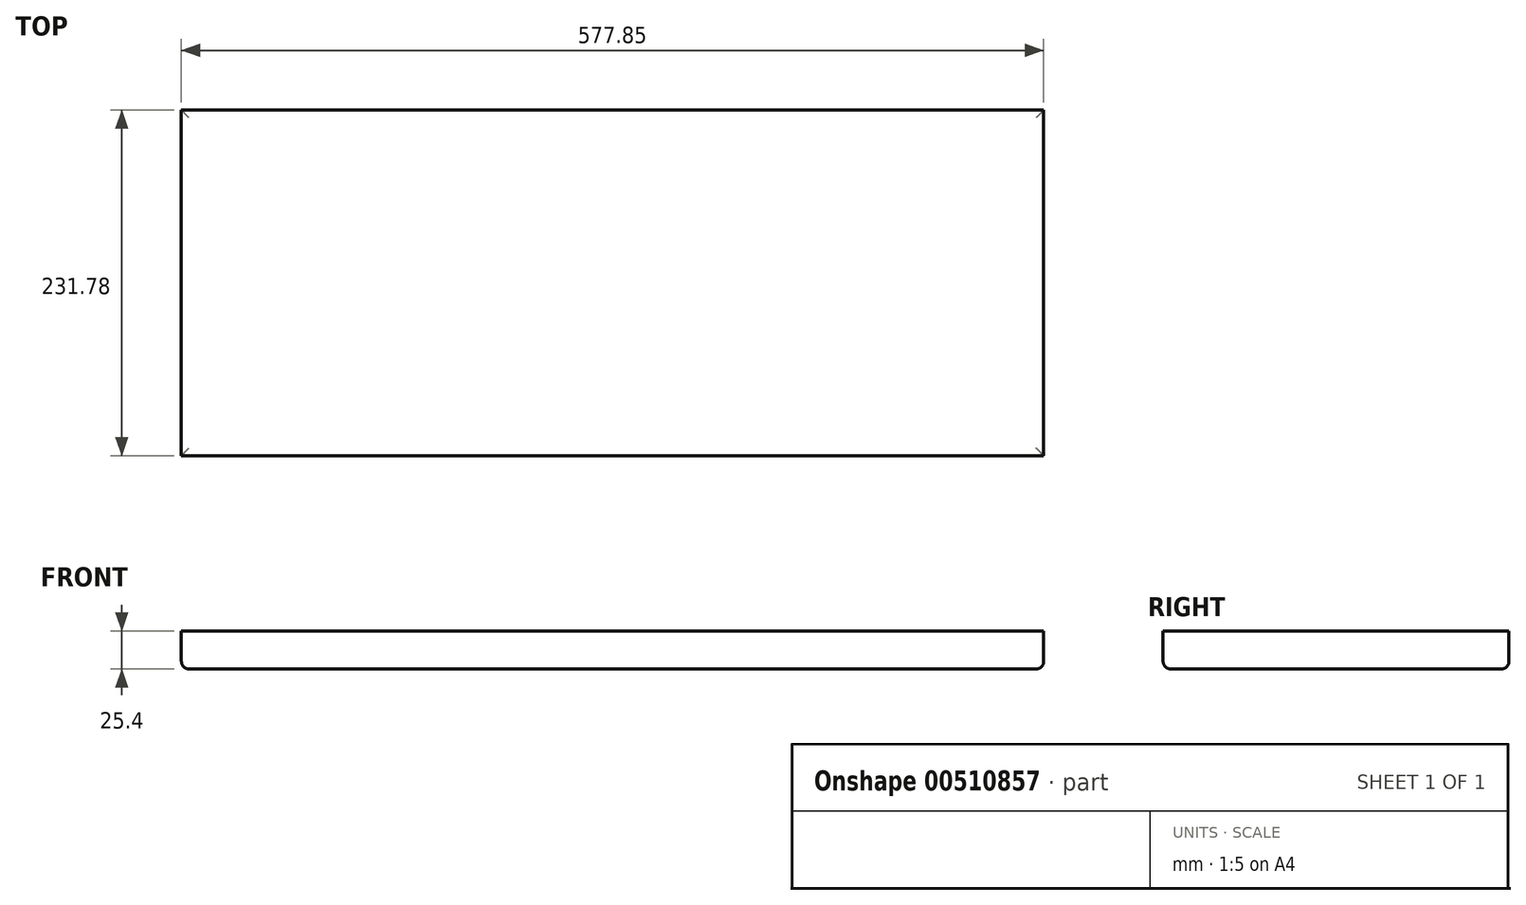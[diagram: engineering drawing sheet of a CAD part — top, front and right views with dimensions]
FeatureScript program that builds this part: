
annotation { "Feature Type Name" : "Feature", "Feature Type Description" : "" }
export const myFeature = defineFeature(function(context is Context, id is Id, definition is map)
    precondition{}
    {
        {
            var Q0;
            Q0=qCreatedBy(makeId("Top.planeOp"),FACE);
            var sketch = newSketch(context, id + "F0", { "sketchPlane" : qUnion([Q0])});
            skLineSegment(sketch, "E0.bottom", {"start": v(-540.1, 213.19) * mm, "end": v(37.75, 213.19) * mm});
            skLineSegment(sketch, "E0.top", {"start": v(-540.1, -18.59) * mm, "end": v(37.75, -18.59) * mm});
            skLineSegment(sketch, "E0.left", {"start": v(-540.1, 213.19) * mm, "end": v(-540.1, -18.59) * mm});
            skLineSegment(sketch, "E0.right", {"start": v(37.75, 213.19) * mm, "end": v(37.75, -18.59) * mm});
            skSolve(sketch);
        }
        {
            var Q0;
            Q0=makeQuery(id+"F0.imprint","IMPRINT",FACE,{"disambiguationData":[TD([[makeQuery(id+"F0.imprint","IMPRINT",EDGE,{"derivedFrom":sQuery(id+"F0.wireOp",EDGE,"E0.bottom")}),-1.0]])]});
            extrude(context, id + "F1", {"entities" : qUnion([Q0]), "depth" : 25.4 * mm, "offsetDistance" : 25.4 * mm});
        }
        {
            var Q0;
            Q0=makeQuery(id+"F1.opExtrude","CAP_EDGE",EDGE,{"disambiguationData":[OSD([sQuery(id+"F0.wireOp",EDGE,"E0.top")])],"isStart":true});
            var Q1;
            Q1=makeQuery(id+"F1.opExtrude","CAP_EDGE",EDGE,{"disambiguationData":[OSD([sQuery(id+"F0.wireOp",EDGE,"E0.right")])],"isStart":true});
            var Q2;
            Q2=makeQuery(id+"F1.opExtrude","CAP_EDGE",EDGE,{"disambiguationData":[OSD([sQuery(id+"F0.wireOp",EDGE,"E0.bottom")])],"isStart":true});
            var Q3;
            Q3=makeQuery(id+"F1.opExtrude","CAP_EDGE",EDGE,{"disambiguationData":[OSD([sQuery(id+"F0.wireOp",EDGE,"E0.left")])],"isStart":true});
            fillet(context, id + "F2", {"entities" : qUnion([Q0, Q1, Q2, Q3]), "radius" : 5.08 * mm, "tangentPropagation" : true, "allowEdgeOverflow" : false});
        }
    });
